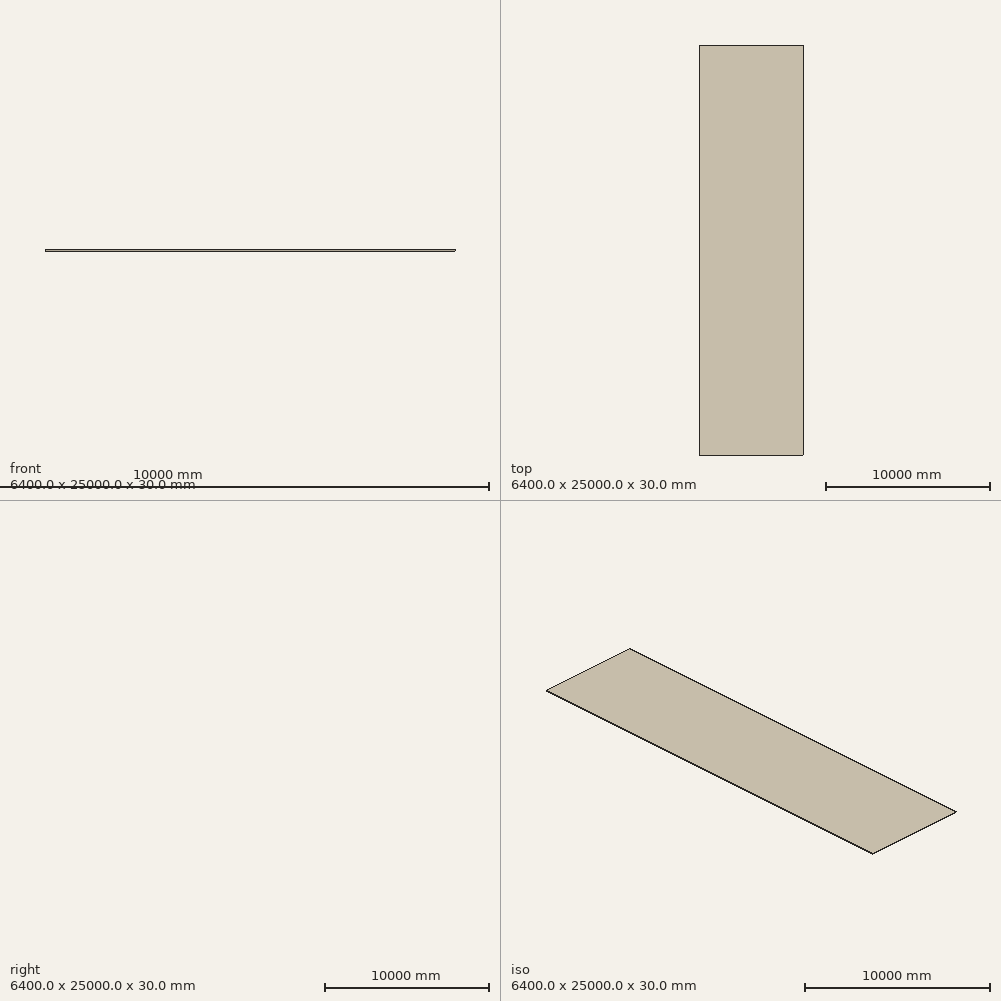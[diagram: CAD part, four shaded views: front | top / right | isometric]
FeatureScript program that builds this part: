
annotation { "Feature Type Name" : "Feature", "Feature Type Description" : "" }
export const myFeature = defineFeature(function(context is Context, id is Id, definition is map)
    precondition{}
    {
        {
            var Q0;
            Q0=qCreatedBy(makeId("Right.planeOp"),FACE);
            var sketch = newSketch(context, id + "F0", { "sketchPlane" : qUnion([Q0])});
            skLineSegment(sketch, "E0.bottom", {"start": v(-120.92, 44.1) * mm, "end": v(24879.08, 44.1) * mm});
            skLineSegment(sketch, "E0.top", {"start": v(-120.92, 14.1) * mm, "end": v(24879.08, 14.1) * mm});
            skLineSegment(sketch, "E0.left", {"start": v(-120.92, 44.1) * mm, "end": v(-120.92, 14.1) * mm});
            skLineSegment(sketch, "E0.right", {"start": v(24879.08, 44.1) * mm, "end": v(24879.08, 14.1) * mm});
            skSolve(sketch);
        }
        {
            var Q0;
            Q0=makeQuery(id+"F0.imprint","IMPRINT",FACE,{"disambiguationData":[TD([[makeQuery(id+"F0.imprint","IMPRINT",EDGE,{"derivedFrom":sQuery(id+"F0.wireOp",EDGE,"E0.bottom")}),-1.0]])]});
            extrude(context, id + "F1", {"entities" : qUnion([Q0]), "depth" : 6400 * mm, "offsetDistance" : 25 * mm});
        }
    });
